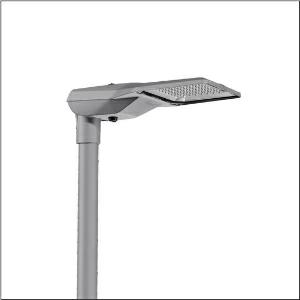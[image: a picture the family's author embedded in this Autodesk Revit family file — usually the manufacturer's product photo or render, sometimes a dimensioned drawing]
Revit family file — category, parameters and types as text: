
# Revit family: streetlight_sl_21_iq_midi___st1_0a_5xe3d51y08nb_3932
name_source: partatom
category: Lighting Fixtures
units: mm (PartAtom-declared; Revit-internal decimal feet)

## family parameters
Cut with Voids When Loaded = No
Host = Face
Light Source = No
Part Type = Normal
Room Calculation Point = No
Round Connector Dimension = Use Diameter
Shared = No

## types (1)
- --- (1 x LED, 18920 lm, 136.6 W, 3000K)
    Apparent Load = 137 VA
    CIE Flux Codes = 40 73 97 100 100
    Color Rendering = 80
    Color Temperature = 3000K
    Default Elevation = 1800 mm
    Description = Streetlight SL 21 iQ midi, mast luminaire, primary light control with lens, of PMMA, primary optical cover: cover, of toughened safety glass, transparent, light distribution: ST1.0a, light emission: direct distribution, primary light characteristic: asymmetric, installation type: post-top, side-entry, LED, High Power LED, rated luminous flux: 18.920lm, luminous efficacy: 139lm/W, light colour: 830, colour temperature: 3000K, control: presetting dimming logarithmic, Street-Remote, Auto-Match, Temp-Guard, Lumen-Switch, Night-Set, Smart-Wire, Light-Fading, Desk-Remote (wireless, voltage-free reading and setting of iQ features in the workshop via application-optimized NFC function/RFID function), optimised constant luminous flux control (CLO 2.0), mains connection: 230..240V, AC, 50/60Hz, start of lifetime: 137W, end of service life: 144W, reduction: 61W, luminaire housing, of diecast aluminium, powder-coated, Siteco® metallic grey (DB 702S), corrosivity category C5 mid according to DIN EN ISO 12944, please order mast flange separately, inclination adjustable: 0°, 5°, 10°, 15°, sealing non-destructively replaceable, multi-level sealing system, length: 644mm, width: 335mm, height: 110mm, mast flange for spigot size: 42mm (side-entry): 5XC10008XM4, 60/48mm (side-entry/post-top): 5XC10108XM2, 76/60mm (side-entry/post-top): 5XC10108XM1, Smart Interface below and above, protection rating (complete): IP66, insulation class (complete): insulation class II (safety insulation), certification: CE, ENEC, ENEC+, VDE, impact resistance: IK09, permissible operating ambient temperature for outdoor applications: -40..+50°C, standard-compliant lighting for roads and squares, packaging unit: 1 piece

Light Distribution: ST1.0a
    Height = 111 mm
    Lamp = 1 x LED
    Lamp Light Flux = 18920 lm
    Lamp Power = 136.6 W
    Lamp count = 1
    Length = 644 mm
    Luminous efficacy = 139 lm/W
    Manufacturer = Siteco
    ModVariant = No
    Model = 5XE3D51Y08NB
    Number of Poles = 1
    OnlyDefault = Yes
    Power Factor = 1
    Product Name = Streetlight SL 21 iQ midi | ST1.0a
    Product group = mast luminaire | pylon top
    ProductGroupID = 6100
    Protection Class = Protection class II
    Protection Degree = IP 66
    RLX_Detail_Level = 1
    RLX_Emergency_Light_Flux = 0 lm
    RLX_Emergency_Type = 0
    RLX_Emergency_Type_DB = No
    RlxData = <blob elided: 92213 chars, md5=142cd8be>
    Socket = socket
    Standby Power = 0 W
    System Light Flux = 18920 lm
    System Power = 137 W
    Type Comments = factory setting: luminous flux: 100 % | dim-lin: 254 | 733 mA
    Type Image = l_1004304.jpg
    URL = http://relux.com
    VarID = @adj_043807
    Voltage = 0 V
    Weight = 0.00 kg
    Width = 336 mm

## geometry (parser evidence)
native form markers: Blend x4, Sweep x10
no freeform markers — native parametric forms only
